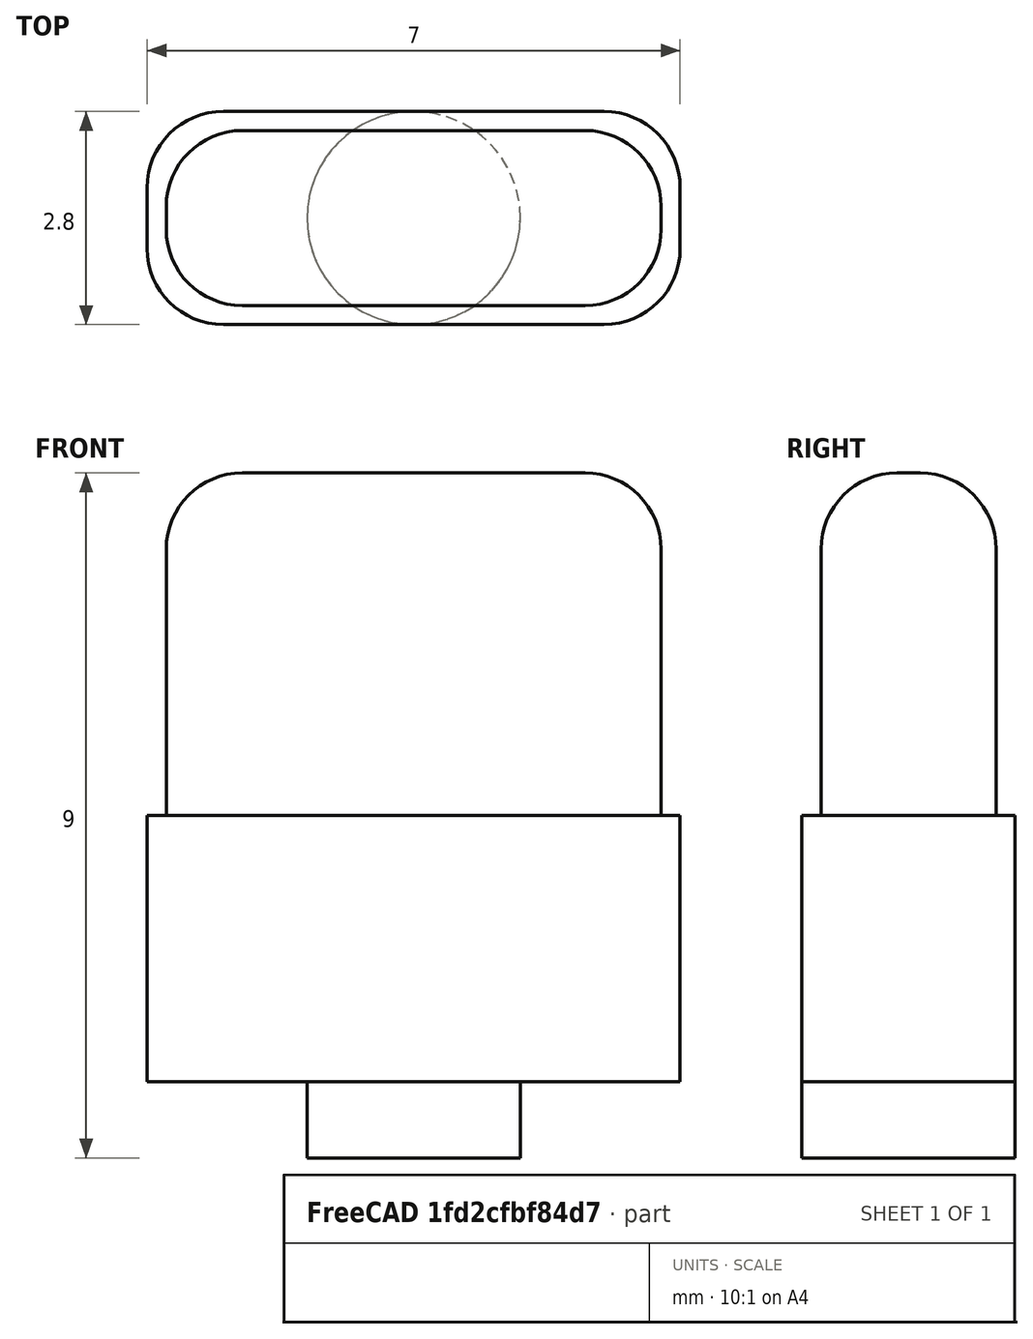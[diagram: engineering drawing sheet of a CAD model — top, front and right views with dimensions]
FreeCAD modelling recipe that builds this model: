
FCSTD DOCUMENT  (FreeCAD 1.0R38642 (Git))
Label: GBC_dome_start_select
License: All rights reserved
LicenseURL: http://en.wikipedia.org/wiki/All_rights_reserved
objects: Part::Box×2, Part::Fillet×2, Part::Cylinder×1, Part::MultiFuse×1
note: 6 computed .brp shape members not serialized (recipe doc carries the construction recipe); baked Part::Feature solids carry a one-line shape summary decoded from their .brp

FEATURE [Part::Box] Box  label="Cube"
  AttacherType = Attacher::AttachEngine3D
  Height = 6
  Length = 6.5
  Width = 2.3
FEATURE [Part::Fillet] Fillet
  Base = -> Box
  EdgeLinks = -> Box [Edge1,Edge2,Edge3,Edge5,Edge6,Edge7,Edge10,Edge12]
  Edges = 8 edges r=1: [Edge1,Edge2,Edge3,Edge5,Edge6,Edge7,Edge10,Edge12]
FEATURE [Part::Box] Box001  label="Cube001"
  AttacherType = Attacher::AttachEngine3D
  Height = 3.5
  Length = 7
  Placement = pos=(-0.25,-0.25,-2) rot=(0,0,1;0rad)
  Width = 2.8
FEATURE [Part::Fillet] Fillet001
  Base = -> Box001
  EdgeLinks = -> Box001 [Edge1,Edge3,Edge5,Edge7]
  Edges = 4 edges r=1: [Edge1,Edge3,Edge5,Edge7]
FEATURE [Part::Cylinder] Cylinder
  Angle = 360
  AttacherType = Attacher::AttachEngine3D
  FirstAngle = 0
  Height = 1
  Placement = pos=(3.25,1.15,-3) rot=(0,0,1;0rad)
  Radius = 1.4
  SecondAngle = 0
FEATURE [Part::MultiFuse] Fusion
  Shapes = -> [Fillet,Fillet001,Cylinder]
